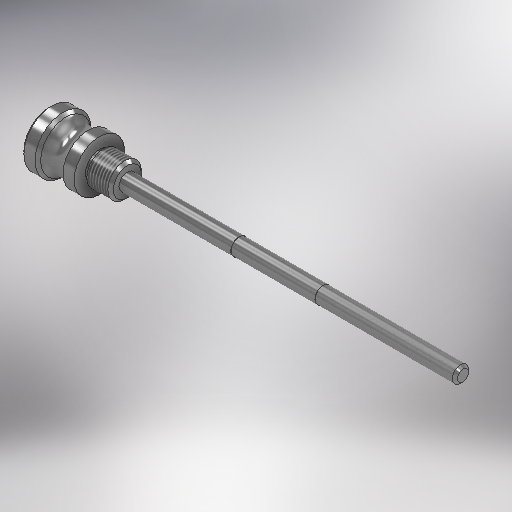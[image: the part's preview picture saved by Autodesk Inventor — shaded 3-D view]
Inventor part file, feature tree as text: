
AUTODESK INVENTOR PART (.ipt)
format: ipt  version: 2025 (Build 290162000, 162)  size: 410,112 bytes
history: native  units: in
note: dims shown in document units (in); Inventor stores cm internally (conversion verified against a paired STEP export)
features: sketch x3, plane x2, extrude x2, revolve x1, thread x1
ambient origin geometry x8: Origin, YZ Plane, XZ Plane, XY Plane, X Axis, Y Axis, Z Axis, Center Point
bodies: 实体1 (feature_tree)
feature tree (9):
  revolve  "旋转1"  [1 undecoded]
  thread  "螺纹1"  [1 undecoded]
  plane  "工作平面1"
  extrude  "拉伸1"  TaperAngle=45.0deg  [1 undecoded]
  plane  "工作平面2"
  extrude  "拉伸2"  Depth=0.2362in
  sketch  "草图1"  dims[d1=0.1575in d2=0.4724in d3=0.2362in d0=0.3937in d4=45.0deg]
  sketch  "草图2"  dims[d5=0.0394in d6=45.0deg]
  sketch  "草图3"  dims[d7=0.0394in d8=0.2362in d9=0.2362in d10=45.0deg d11=0.0394in d12=0.1181in d13=0.1575in d14=0.3937in d16=1.1024in d17=0.3543in d18=0.0591in d19=0.0394in d20=90.0deg d21=45.0deg d22=0.0394in d23=5.1181in d24=0.2953in d25=0.0in d26=-1.9685in d27=0.2283in d28=0.0in d29=0.0in d30=0.2362in d31=-3.1496in d32=0.2323in d33=0.2362in d34=0.0in d35=0.0in]
note: 3 required parameter values undecoded (feature->parameter linkage not recoverable at this tier; creation-order binding heuristic only, values carry confidence <= 0.55)